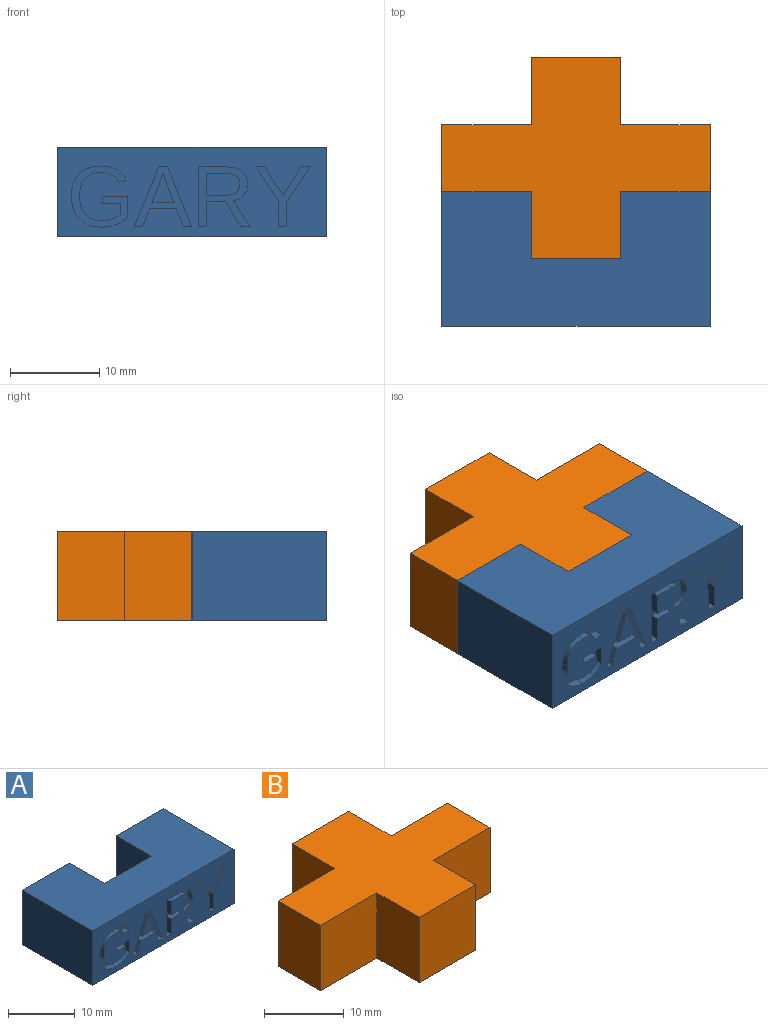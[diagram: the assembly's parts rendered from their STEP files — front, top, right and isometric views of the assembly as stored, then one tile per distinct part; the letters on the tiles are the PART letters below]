
ASSEMBLY  parts=2 mates=1
PART A: 82 faces, bbox 30x15x10 mm
  f0: plane 30x10mm, normal (0,-1,0), area 232.7mm2, adj f1,f2,f8,f9,f10,f11,f12,f13
  f1: plane 15x10mm, normal (-1,0,0), area 150mm2, adj f0,f7,f8,f9
  f2: plane 15x10mm, normal (1,0,0), area 150mm2, adj f0,f3,f8,f9
  f3: plane 10x10mm, normal (0,1,0), area 100mm2, adj f2,f4,f8,f9
  f4: plane 10x7.5mm, normal (-1,0,0), area 75mm2, adj f3,f5,f8,f9
  f5: plane 10x10mm, normal (0,1,0), area 100mm2, adj f4,f6,f8,f9
  f6: plane 10x7.5mm, normal (1,0,0), area 75mm2, adj f5,f7,f8,f9
  f7: plane 10x10mm, normal (0,1,0), area 100mm2, adj f1,f6,f8,f9
  f8: plane 30x15mm, normal (0,0,1), area 375mm2, adj f0,f1,f2,f3,f4,f5,f6,f7
  f9: plane 30x15mm, normal (0,0,-1), area 375mm2, adj f0,f1,f2,f3,f4,f5,f6,f7
  f10: plane 2.75x1mm, normal (-1,0,0), area 2.8mm2, adj f0,f11,f18,f19
  f11: plane 3.89x2.56mm, normal (-0.83,0,0.55), area 4.7mm2, adj f0,f10,f12,f19
  f12: plane 1x0.99mm, normal (0,0,-1), area 1mm2, adj f0,f11,f13,f19
  f13: plane 3.16x2.01mm, normal (0.84,0,-0.54), area 3.7mm2, adj f0,f12,f14,f19
  f14: plane 3.16x2.02mm, normal (-0.84,0,-0.54), area 3.8mm2, adj f0,f13,f15,f19
  f15: plane 1x0.99mm, normal (0,0,-1), area 1mm2, adj f0,f14,f16,f19
  f16: plane 3.89x2.55mm, normal (0.84,0,0.55), area 4.7mm2, adj f0,f15,f17,f19
  f17: plane 2.75x1mm, normal (1,0,0), area 2.8mm2, adj f0,f16,f18,f19
  f18: plane 1x0.9mm, normal (0,0,1), area 0.9mm2, adj f0,f10,f17,f19
  f19: plane 6.64x6.01mm, normal (0,-1,0), area 9.5mm2, adj f10,f11,f12,f13,f14,f15,f16,f17
  f20: plane 1x0.13mm, normal (-0.95,0,0.31), area 0.1mm2, adj f21,f34,f35,f80
  f21: plane 1x0.39mm, normal (0.95,0,0.31), area 0.4mm2, adj f20,f22,f35,f80
  f22: extruded ~1x0.74mm, area 0.8mm2, adj f21,f23,f35,f80
  f23: plane 2.19x1mm, normal (0.93,0,0.36), area 2.4mm2, adj f22,f24,f35,f80
  f24: plane 2.48x1mm, normal (0,0,-1), area 2.5mm2, adj f23,f25,f35,f80
  f25: plane 2.18x1mm, normal (-0.93,0,0.36), area 2.3mm2, adj f24,f34,f35,f80
  f26: plane 1.94x1mm, normal (0.93,0,0.36), area 2.1mm2, adj f0,f27,f33,f35
  f27: plane 1x0.92mm, normal (0,0,1), area 0.9mm2, adj f0,f26,f28,f35
  f28: plane 6.64x2.67mm, normal (-0.93,0,-0.37), area 7.2mm2, adj f0,f27,f29,f35
  f29: plane 1.02x1mm, normal (0,0,-1), area 1mm2, adj f0,f28,f30,f35
  f30: plane 6.64x2.71mm, normal (0.93,0,-0.38), area 7.2mm2, adj f0,f29,f31,f35
  f31: plane 1x0.93mm, normal (0,0,1), area 0.9mm2, adj f0,f30,f32,f35
  f32: plane 1.94x1mm, normal (-0.93,0,0.37), area 2.1mm2, adj f0,f31,f33,f35
  f33: plane 3.03x1mm, normal (0,0,1), area 3mm2, adj f0,f26,f32,f35
  f34: extruded ~1x1mm, area 1.1mm2, adj f20,f25,f35,f80
  f35: plane 6.64x6.4mm, normal (0,-1,0), area 13.3mm2, adj f20,f21,f22,f23,f24,f25,f26,f27
  f36: extruded ~1x0.88mm, area 1mm2, adj f37,f54,f55,f81
  f37: extruded ~1x0.93mm, area 1mm2, adj f36,f38,f55,f81
  f38: extruded ~1.1x1mm, area 1.2mm2, adj f37,f39,f55,f81
  f39: plane 2.17x1mm, normal (0,0,-1), area 2.2mm2, adj f38,f40,f55,f81
  f40: plane 2.45x1mm, normal (-1,0,0), area 2.5mm2, adj f39,f41,f55,f81
  f41: plane 2.14x1mm, normal (0,0,1), area 2.1mm2, adj f40,f54,f55,f81
  f42: plane 2.76x1.73mm, normal (0.85,0,0.53), area 3.3mm2, adj f0,f43,f53,f55
  f43: plane 1.04x1mm, normal (0,0,1), area 1mm2, adj f0,f42,f44,f55
  f44: plane 2.86x1.89mm, normal (-0.84,0,-0.55), area 3.4mm2, adj f0,f43,f45,f55
  f45: extruded ~1.19x1mm, area 1.4mm2, adj f0,f44,f46,f55
  f46: extruded ~1.25x1mm, area 1.3mm2, adj f0,f45,f47,f55
  f47: extruded ~1.4x1mm, area 1.6mm2, adj f0,f46,f48,f55
  f48: extruded ~1.73x1mm, area 1.8mm2, adj f0,f47,f49,f55
  f49: plane 3.13x1mm, normal (0,0,-1), area 3.1mm2, adj f0,f48,f50,f55
  f50: plane 6.64x1mm, normal (1,0,0), area 6.6mm2, adj f0,f49,f51,f55
  f51: plane 1x0.9mm, normal (0,0,1), area 0.9mm2, adj f0,f50,f52,f55
  f52: plane 2.76x1mm, normal (-1,0,0), area 2.8mm2, adj f0,f51,f53,f55
  f53: plane 2.07x1mm, normal (0,0,1), area 2.1mm2, adj f0,f42,f52,f55
  f54: extruded ~1.13x1mm, area 1.2mm2, adj f36,f41,f55,f81
  f55: plane 6.64x5.73mm, normal (0,-1,0), area 16.5mm2, adj f36,f37,f38,f39,f40,f41,f42,f43
  f56: extruded ~2.5x1mm, area 2.7mm2, adj f0,f57,f78,f79
  f57: extruded ~1.84x1mm, area 1.9mm2, adj f0,f56,f58,f79
  f58: extruded ~1.2x1.15mm, area 1.7mm2, adj f0,f57,f59,f79
  f59: extruded ~1.8x1mm, area 1.9mm2, adj f0,f58,f60,f79
  f60: extruded ~1.66x1mm, area 1.7mm2, adj f0,f59,f61,f79
  f61: extruded ~1.29x1mm, area 1.6mm2, adj f0,f60,f62,f79
  f62: plane 2.29x1mm, normal (-1,0,0), area 2.3mm2, adj f0,f61,f63,f79
  f63: plane 2.81x1mm, normal (0,0,-1), area 2.8mm2, adj f0,f62,f64,f79
  f64: plane 1x0.75mm, normal (1,0,0), area 0.8mm2, adj f0,f63,f65,f79
  f65: plane 1.99x1mm, normal (0,0,1), area 2mm2, adj f0,f64,f66,f79
  f66: plane 1.2x1mm, normal (1,0,0), area 1.2mm2, adj f0,f65,f67,f79
  f67: extruded ~1x0.91mm, area 1.1mm2, adj f0,f66,f68,f79
  f68: extruded ~1.21x1mm, area 1.2mm2, adj f0,f67,f69,f79
  f69: extruded ~1.79x1mm, area 2mm2, adj f0,f68,f70,f79
  f70: extruded ~1.99x1mm, area 2.1mm2, adj f0,f69,f71,f79
  f71: extruded ~1.96x1mm, area 2.1mm2, adj f0,f70,f72,f79
  f72: extruded ~1.76x1mm, area 2mm2, adj f0,f71,f73,f79
  f73: extruded ~1.24x1mm, area 1.3mm2, adj f0,f72,f74,f79
  f74: extruded ~1x0.82mm, area 1.2mm2, adj f0,f73,f75,f79
  f75: plane 1x0.86mm, normal (-0.28,0,0.96), area 0.9mm2, adj f0,f74,f76,f79
  f76: extruded ~1.19x1.06mm, area 1.6mm2, adj f0,f75,f77,f79
  f77: extruded ~1.79x1mm, area 1.8mm2, adj f0,f76,f78,f79
  f78: extruded ~2.44x1mm, area 2.7mm2, adj f0,f56,f77,f79
  f79: plane 6.84x6.3mm, normal (0,-1,0), area 15.7mm2, adj f56,f57,f58,f59,f60,f61,f62,f63
  f80: plane 3.32x2.48mm, normal (0,-1,0), area 4mm2, adj f20,f21,f22,f23,f24,f25,f34
  f81: plane 3.66x2.45mm, normal (0,-1,0), area 8.3mm2, adj f36,f37,f38,f39,f40,f41,f54
PART B: 14 faces, bbox 30x22.5x10 mm
  f0: plane 10x7.5mm, normal (-1,0,0), area 75mm2, adj f1,f11,f12,f13
  f1: plane 10x10mm, normal (0,-1,0), area 100mm2, adj f0,f2,f12,f13
  f2: plane 10x7.5mm, normal (1,0,0), area 75mm2, adj f1,f3,f12,f13
  f3: plane 10x10mm, normal (0,-1,0), area 100mm2, adj f2,f4,f12,f13
  f4: plane 10x7.5mm, normal (1,0,0), area 75mm2, adj f3,f5,f12,f13
  f5: plane 10x10mm, normal (0,1,0), area 100mm2, adj f4,f6,f12,f13
  f6: plane 10x7.5mm, normal (1,0,0), area 75mm2, adj f5,f7,f12,f13
  f7: plane 10x10mm, normal (0,1,0), area 100mm2, adj f6,f8,f12,f13
  f8: plane 10x7.5mm, normal (-1,0,0), area 75mm2, adj f7,f9,f12,f13
  f9: plane 10x10mm, normal (0,1,0), area 100mm2, adj f8,f10,f12,f13
  f10: plane 10x7.5mm, normal (-1,0,0), area 75mm2, adj f9,f11,f12,f13
  f11: plane 10x10mm, normal (0,-1,0), area 100mm2, adj f0,f10,f12,f13
  f12: plane 30x22.5mm, normal (0,0,1), area 375mm2, adj f0,f1,f2,f3,f4,f5,f6,f7
  f13: plane 30x22.5mm, normal (0,0,-1), area 375mm2, adj f0,f1,f2,f3,f4,f5,f6,f7
PLACE A t=(-25.91,-10.79,-7.64)mm
PLACE B t=(-26.91,-12.05,-7.64)mm
MATE fastened B.f1 <-> A.f5  axis (0,-1,0) through (-25.51,-16.49,2.36)mm
